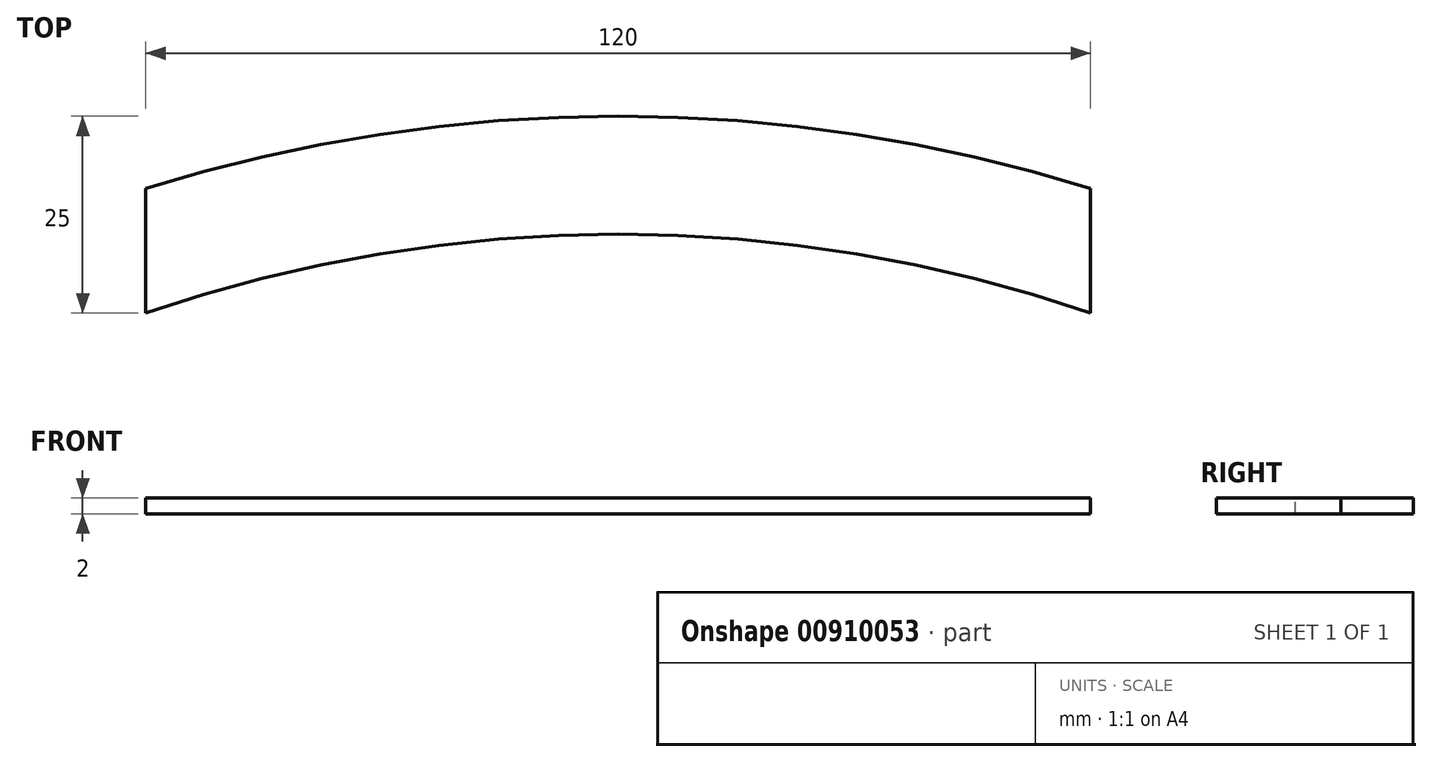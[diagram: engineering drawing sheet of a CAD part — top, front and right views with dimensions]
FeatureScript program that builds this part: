
annotation { "Feature Type Name" : "Feature", "Feature Type Description" : "" }
export const myFeature = defineFeature(function(context is Context, id is Id, definition is map)
    precondition{}
    {
        {
            var Q0;
            Q0=qCreatedBy(makeId("Top.planeOp"),FACE);
            var sketch = newSketch(context, id + "F0", { "sketchPlane" : qUnion([Q0])});
            skCircle(sketch, "E0", {"center": v(0, 0) * mm, "radius": 200 * mm});
            skSolve(sketch);
        }
        {
            var Q0;
            Q0=makeQuery(id+"F0.imprint","IMPRINT",FACE,{"disambiguationData":[TD([[makeQuery(id+"F0.imprint","IMPRINT",EDGE,{"derivedFrom":sQuery(id+"F0.wireOp",EDGE,"E0")}),1.0]])]});
            extrude(context, id + "F1", {"entities" : qUnion([Q0]), "depth" : 2 * mm, "offsetDistance" : 25 * mm});
        }
        {
            var Q0;
            Q0=makeQuery(id+"F1.opExtrude","CAP_FACE",FACE,{"disambiguationData":[OSD([sQuery(id+"F0.wireOp",EDGE,"E0")])],"isStart":false});
            var sketch = newSketch(context, id + "F2", { "sketchPlane" : qUnion([Q0])});
            skCircle(sketch, "E1.0", {"center": v(0, 0) * mm, "radius": 185 * mm});
            skLineSegment(sketch, "E2", {"start": v(0, 185) * mm, "end": v(0, 200) * mm});
            skLineSegment(sketch, "E3", {"start": v(-60, 175) * mm, "end": v(-60, 190.79) * mm});
            skLineSegment(sketch, "E4", {"start": v(60, 175) * mm, "end": v(60, 190.79) * mm});
            skSolve(sketch);
        }
        {
            var Q0;
            {var subQ0=sQuery(id+"F2.wireOp",EDGE,"E1.0");var subQ1=makeQuery(id+"F2.imprint","INTERSECT",VERTEX,{"derivedFrom":[subQ0,sQuery(id+"F2.wireOp",EDGE,"E2")]});Q0=makeQuery(id+"F2.imprint","IMPRINT",FACE,{"disambiguationData":[TD([[makeQuery(id+"F2.imprint","IMPRINT",EDGE,{"disambiguationData":[TD([[subQ1,1.0]])],"derivedFrom":subQ0}),1.0]])]});}
            var Q1;
            {var subQ0=sQuery(id+"F2.wireOp",EDGE,"E3");Q1=makeQuery(id+"F2.imprint","IMPRINT",FACE,{"disambiguationData":[TD([[makeQuery(id+"F2.imprint","IMPRINT",EDGE,{"derivedFrom":subQ0}),1.0]])]});}
            extrude(context, id + "F3", {"entities" : qUnion([Q0, Q1]), "operationType" : NewBodyOperationType.REMOVE, "oppositeDirection" : true, "depth" : 25 * mm, "offsetDistance" : 25 * mm});
        }
    });
